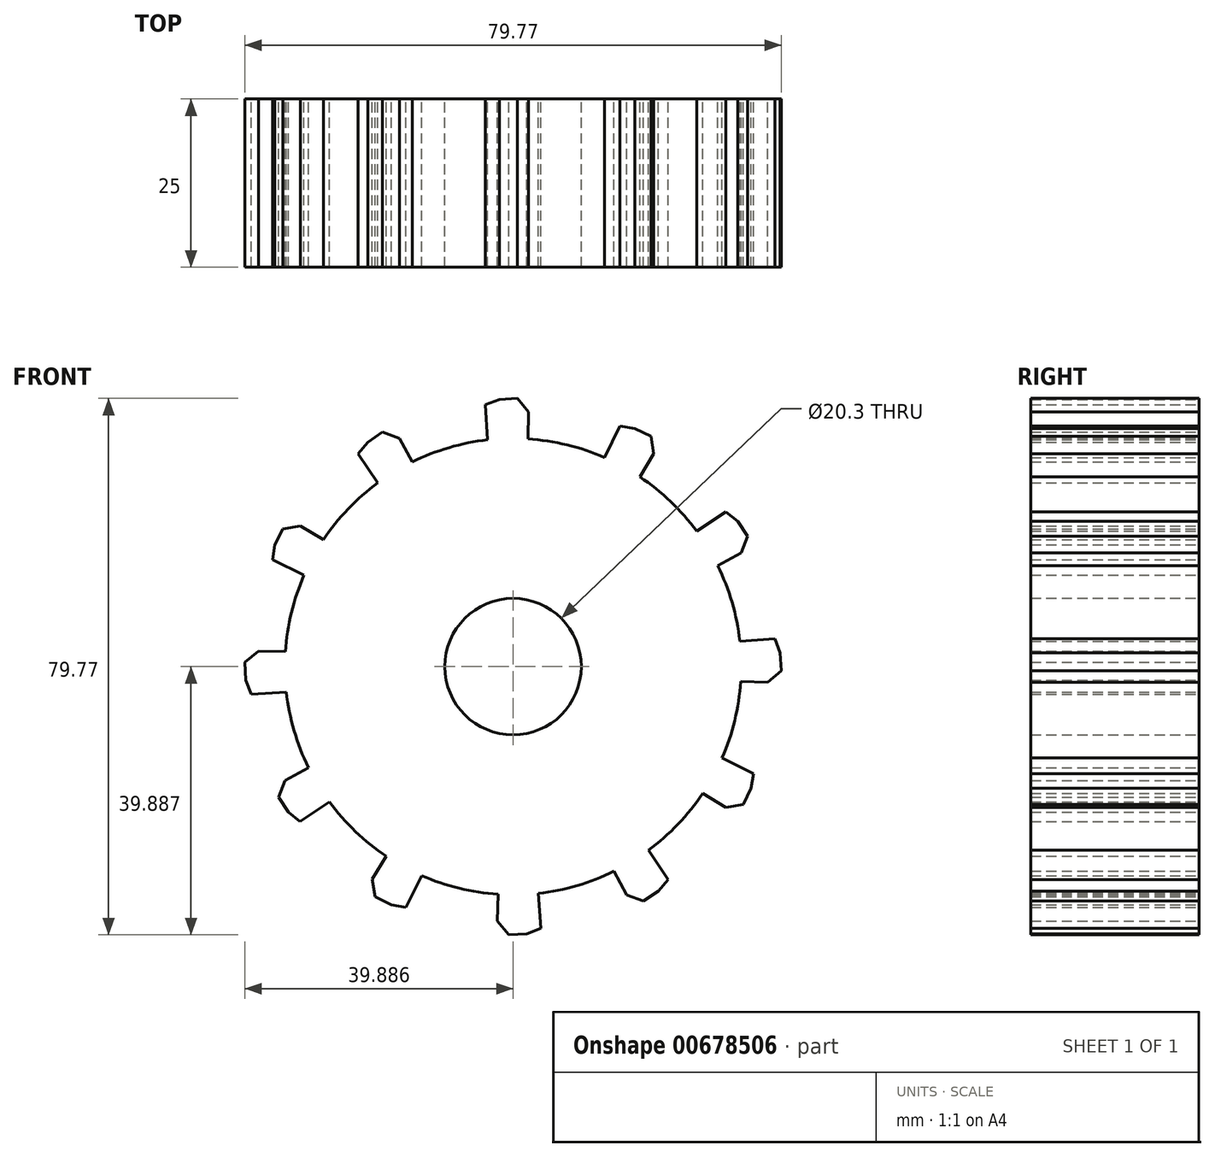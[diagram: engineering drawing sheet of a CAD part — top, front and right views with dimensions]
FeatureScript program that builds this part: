
annotation { "Feature Type Name" : "Feature", "Feature Type Description" : "" }
export const myFeature = defineFeature(function(context is Context, id is Id, definition is map)
    precondition{}
    {
        {
            var Q0;
            Q0=qCreatedBy(makeId("Front.planeOp"),FACE);
            var sketch = newSketch(context, id + "F0", { "sketchPlane" : qUnion([Q0])});
            skArc(sketch, "E0", {"start": v(0.08, 53.96) * mm, "mid": v(-0.8, 53.94) * mm, "end": v(-1.68, 53.9) * mm, "construction": true});
            skCircle(sketch, "E1", {"center": v(0.08, 27.1) * mm, "radius": 29.34 * mm, "construction": true});
            skCircle(sketch, "E2", {"center": v(0.08, 27.1) * mm, "radius": 31.75 * mm, "construction": true});
            skLineSegment(sketch, "E3", {"start": v(0.08, 27.1) * mm, "end": v(0.08, 62.45) * mm, "construction": true});
            skLineSegment(sketch, "E4", {"start": v(0.08, 27.1) * mm, "end": v(-1.37, 49.08) * mm, "construction": true});
            skLineSegment(sketch, "E5", {"start": v(-7.47, 54.84) * mm, "end": v(-8.89, 54.45) * mm, "construction": true});
            skArc(sketch, "E6", {"start": v(-8.88, 54.42) * mm, "mid": v(8.33, -0.45) * mm, "end": v(-7.47, 54.84) * mm, "construction": true});
            skArc(sketch, "E7", {"start": v(28.83, 27.1) * mm, "mid": v(17.54, 49.94) * mm, "end": v(-7.47, 54.84) * mm});
            skCircle(sketch, "E8", {"center": v(0.08, 27.1) * mm, "radius": 25.1 * mm});
            skCircle(sketch, "E9", {"center": v(-1.84, 56.37) * mm, "radius": 7.3 * mm, "construction": true});
            skLineSegment(sketch, "E10", {"start": v(0.06, 56.43) * mm, "end": v(-39.81, 61.63) * mm, "construction": true});
            skLineSegment(sketch, "E11", {"start": v(0.06, 56.43) * mm, "end": v(-37.23, 48.11) * mm, "construction": true});
            skArc(sketch, "E12.trimOffspring", {"start": v(-1.71, 55.8) * mm, "mid": v(-2.8, 56.42) * mm, "end": v(-3.94, 56.95) * mm, "construction": true});
            skArc(sketch, "E13.trimOffspring", {"start": v(-15.7, 51.83) * mm, "mid": v(-15.59, 51.56) * mm, "end": v(-15.47, 51.28) * mm, "construction": true});
            skCircle(sketch, "E14", {"center": v(-8.88, 54.42) * mm, "radius": 7.3 * mm, "construction": true});
            skArc(sketch, "E15", {"start": v(-1.71, 55.8) * mm, "mid": v(-2.24, 57.29) * mm, "end": v(-2.96, 58.7) * mm});
            skArc(sketch, "E16", {"start": v(-1.68, 53.9) * mm, "mid": v(-1.66, 53.68) * mm, "end": v(-1.64, 53.46) * mm});
            skPoint(sketch, "E17.orphan", {"position": v(8.08, 61.03) * mm});
            skPoint(sketch, "E18.MirrorCS.start.orphan", {"position": v(5.57, 55.21) * mm});
            skPoint(sketch, "E19.MirrorCS.start.orphan", {"position": v(5.5, 51.43) * mm});
            skArc(sketch, "E20", {"start": v(-0.68, 61) * mm, "mid": v(0.45, -6.82) * mm, "end": v(0.08, 61.02) * mm});
            skCircle(sketch, "E21", {"center": v(0.08, 27.1) * mm, "radius": 21.7 * mm});
            skPoint(sketch, "E22.start.orphan", {"position": v(-18.72, 27.1) * mm});
            skPoint(sketch, "E23.start.orphan", {"position": v(18.13, 27.1) * mm});
            skPoint(sketch, "E24.end.orphan", {"position": v(-4.89, 48.22) * mm});
            skPoint(sketch, "E25.orphan", {"position": v(-4.89, 13.55) * mm});
            skArc(sketch, "E26.trimOffspring", {"start": v(-1.69, 53.98) * mm, "mid": v(-1.64, 54.02) * mm, "end": v(-1.59, 54.05) * mm});
            skPoint(sketch, "E27.MirrorCS.start.orphan", {"position": v(1.83, 53.9) * mm});
            skPoint(sketch, "E28.trimOffspring.end.orphan", {"position": v(1.86, 55.8) * mm});
            skArc(sketch, "E29.trimOffspring", {"start": v(-1.65, 56.66) * mm, "mid": v(-1.68, 56.22) * mm, "end": v(-1.71, 55.8) * mm});
            skArc(sketch, "E30.trimOffspring", {"start": v(-1.44, 52.15) * mm, "mid": v(-1.4, 51.94) * mm, "end": v(-1.35, 51.72) * mm});
            skLineSegment(sketch, "E31.trimOffspring", {"start": v(-1.57, 52.15) * mm, "end": v(-3.06, 74.9) * mm, "construction": true});
            skLineSegment(sketch, "E32", {"start": v(-2.14, 60.95) * mm, "end": v(-2.24, 62.48) * mm});
            skArc(sketch, "E33.MirrorCS", {"start": v(2.35, 62.35) * mm, "mid": v(2.37, 62.41) * mm, "end": v(2.4, 62.48) * mm});
            skPoint(sketch, "E34.orphan", {"position": v(2.3, 60.95) * mm});
            skArc(sketch, "E35", {"start": v(0.08, 36.33) * mm, "mid": v(-0.23, 36.32) * mm, "end": v(-0.53, 36.3) * mm});
            skLineSegment(sketch, "E36", {"start": v(1.93, 62.62) * mm, "end": v(1.92, 62.59) * mm});
            skPoint(sketch, "E37.end.orphan", {"position": v(-1.77, 62.59) * mm});
            skPoint(sketch, "E38.orphan", {"position": v(-1.66, 61) * mm});
            skLineSegment(sketch, "E39.trimOffspring", {"start": v(0.08, 61) * mm, "end": v(-0.68, 61) * mm});
            skPoint(sketch, "E40.start.orphan", {"position": v(1.8, 61) * mm});
            skLineSegment(sketch, "E41", {"start": v(-2.14, 60.95) * mm, "end": v(-2.2, 61.94) * mm});
            skLineSegment(sketch, "E42", {"start": v(0, 61.92) * mm, "end": v(0.08, 61) * mm});
            skLineSegment(sketch, "E43", {"start": v(-0.17, 62.46) * mm, "end": v(0.08, 62.45) * mm});
            skLineSegment(sketch, "E44.trimOffspring", {"start": v(0.08, 63.42) * mm, "end": v(0.08, 103.12) * mm, "construction": true});
            skPoint(sketch, "E45.end.orphan", {"position": v(-2.14, 62.46) * mm});
            skLineSegment(sketch, "E46", {"start": v(0.08, 61) * mm, "end": v(2.3, 60.95) * mm});
            skLineSegment(sketch, "E47", {"start": v(-3.7, 60.8) * mm, "end": v(-3.87, 63.39) * mm});
            skPoint(sketch, "E48.start.orphan", {"position": v(-3.87, 67.12) * mm});
            skLineSegment(sketch, "E49", {"start": v(-3.87, 63.39) * mm, "end": v(-4.04, 66.03) * mm});
            skLineSegment(sketch, "E50", {"start": v(-4.04, 66.03) * mm, "end": v(-1.95, 66.8) * mm});
            skLineSegment(sketch, "E51", {"start": v(-1.95, 66.8) * mm, "end": v(0.7, 66.98) * mm});
            skLineSegment(sketch, "E52", {"start": v(0.7, 66.98) * mm, "end": v(2.4, 64.93) * mm});
            skLineSegment(sketch, "E53", {"start": v(2.4, 64.93) * mm, "end": v(2.3, 60.95) * mm});
            skCircle(sketch, "E54", {"center": v(0.08, 27.1) * mm, "radius": 10.15 * mm});
            skSolve(sketch);
        }
        {
            var Q0;
            Q0 = qSketchRegion(id + "F0", true);
            var Q1;
            Q1=makeQuery(id+"F0.imprint","IMPRINT",FACE,{"disambiguationData":[TD([[makeQuery(id+"F0.imprint","IMPRINT",EDGE,{"derivedFrom":sQuery(id+"F0.wireOp",EDGE,"E21")}),1.0]])]});
            var Q2;
            Q2=makeQuery(id+"F0.imprint","IMPRINT",FACE,{"disambiguationData":[TD([[makeQuery(id+"F0.imprint","IMPRINT",EDGE,{"derivedFrom":sQuery(id+"F0.wireOp",EDGE,"E8")}),1.0]])]});
            extrude(context, id + "F1", {"entities" : qUnion([Q0, Q1, Q2]), "depth" : 25 * mm, "offsetDistance" : 25 * mm});
        }
        {
            var Q0;
            Q0=makeQuery(id+"F1.opExtrude","SWEPT_BODY",BODY,{"disambiguationData":[OSD([sQuery(id+"F0.wireOp",EDGE,"E20"),sQuery(id+"F0.wireOp",EDGE,"E35"),sQuery(id+"F0.wireOp",EDGE,"E47"),sQuery(id+"F0.wireOp",EDGE,"U65ItQXw-Qiqi-nk2n-s98m-HempwA57eXhe"),sQuery(id+"F0.wireOp",EDGE,"VmdW0ReF-ASdB-8CFZ-peyQ-wq8K9FO15Mj2"),sQuery(id+"F0.wireOp",EDGE,"ymyMHc0b-wpzX-smtr-K1Tn-u2AeGsf0SK1I"),sQuery(id+"F0.wireOp",EDGE,"nNH0LHuy-UW2Z-wEmy-JIhq-fbFNjurpncLa")])]});
            var Q1;
            Q1=makeQuery(id+"F1.opExtrude","SWEPT_FACE",FACE,{"disambiguationData":[OSD([sQuery(id+"F0.wireOp",EDGE,"E20")])]});
            circularPattern(context, id + "F2", {"operationType" : NewBodyOperationType.ADD, "entities" : qUnion([Q0]), "axis" : qUnion([Q1]), "angle" : 360 * degree, "instanceCount" : 12, "equalSpace" : true});
        }
    });
